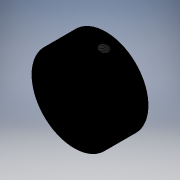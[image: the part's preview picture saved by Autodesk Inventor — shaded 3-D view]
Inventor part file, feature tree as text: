
AUTODESK INVENTOR PART (.ipt)
format: ipt  version: 2017.3 (Build 213256000, 256)  size: 258,560 bytes
history: native  units: mm (DEFAULTED — no unit token found)
features: other x28, sketch x9, revolve x6, pattern_linear x3, hole x2, thread x2, extrude x1
ambient origin geometry x8: Origin, YZ Plane, XZ Plane, XY Plane, X Axis, Y Axis, Z Axis, Center Point
bodies: Solid1 (feature_tree)
feature tree (51):
  revolve  "Revolution1"  Angle=360.0deg
  revolve  "Revolution2"  [1 undecoded]
  pattern_linear  "Rectangular Pattern1"  Count1=2 Spacing1=11.0mm
  extrude  "Extrusion1"  Depth=20.0mm
  pattern_linear  "Rectangular Pattern2"  Spacing1=360.0deg  [1 undecoded]
  hole  "Hole1"  [1 undecoded]
  pattern_linear  "Rectangular Pattern3"  Spacing1=0.0mm  [1 undecoded]
  hole  "Hole2"  [1 undecoded]
  revolve  "Revolution3"  [1 undecoded]
  thread  "Thread1"  [1 undecoded]
  revolve  "Revolution4"  [1 undecoded]
  thread  "Thread2"  [1 undecoded]
  revolve  "Revolution5"  [1 undecoded]
  revolve  "Revolution6"  [1 undecoded]
  other  "ring_stk_XY"
  other  "ring_stk_YZ"
  other  "ring_stk_ZX"
  other  "ring_stk_X"
  other  "ring_stk_Y"
  other  "ring_stk_Z"
  other  "ring_stk_Center"
  other  "stecker_XY"
  other  "stecker_YZ"
  other  "stecker_ZX"
  other  "stecker_X"
  other  "stecker_Y"
  other  "stecker_Z"
  other  "stecker_Center"
  other  "vss1_XY"
  other  "vss1_YZ"
  other  "vss1_ZX"
  other  "vss1_X"
  other  "vss1_Y"
  other  "vss1_Z"
  other  "vss1_Center"
  other  "vss2_XY"
  other  "vss2_YZ"
  other  "vss2_ZX"
  other  "vss2_X"
  other  "vss2_Y"
  other  "vss2_Z"
  other  "vss2_Center"
  sketch  "Sketch_1"  dims[d0=360.0deg d1=360.0deg]
  sketch  "Sketch_2"  dims[d2=20.0mm d4=11.0mm d5=10.0mm d7=0.0mm d8=2.5mm d9=0.0mm d10=20.0mm d12=11.0mm d13=10.0mm d15=0.0mm]
  sketch  "Sketch_7"  dims[d36=360.0deg]
  sketch  "Sketch4"  dims[d16=4.134mm d17=8.433mm d18=5.0mm d19=2.0mm d20=90.0deg d21=11.0mm d22=120.0deg d23=20.0mm d25=28.284271mm d26=20.0mm d28=28.284271mm]
  sketch  "Sketch5"  dims[d29=5.0mm d30=6.0mm d31=4.0mm d32=2.0mm d33=90.0deg d34=5.0mm d35=20.594885mm]
  sketch  "Sketch_9"  dims[d37=6.0mm d38=0.0mm]
  sketch  "Sketch_10"  dims[d39=360.0deg]
  sketch  "Sketch_11"  dims[d40=6.0mm d41=0.0mm]
  sketch  "Sketch_12"  dims[d42=360.0deg d43=360.0deg d44=0.0mm d45=0.0mm d46=0.0mm]
note: 11 required parameter values undecoded (feature->parameter linkage not recoverable at this tier; creation-order binding heuristic only, values carry confidence <= 0.55)